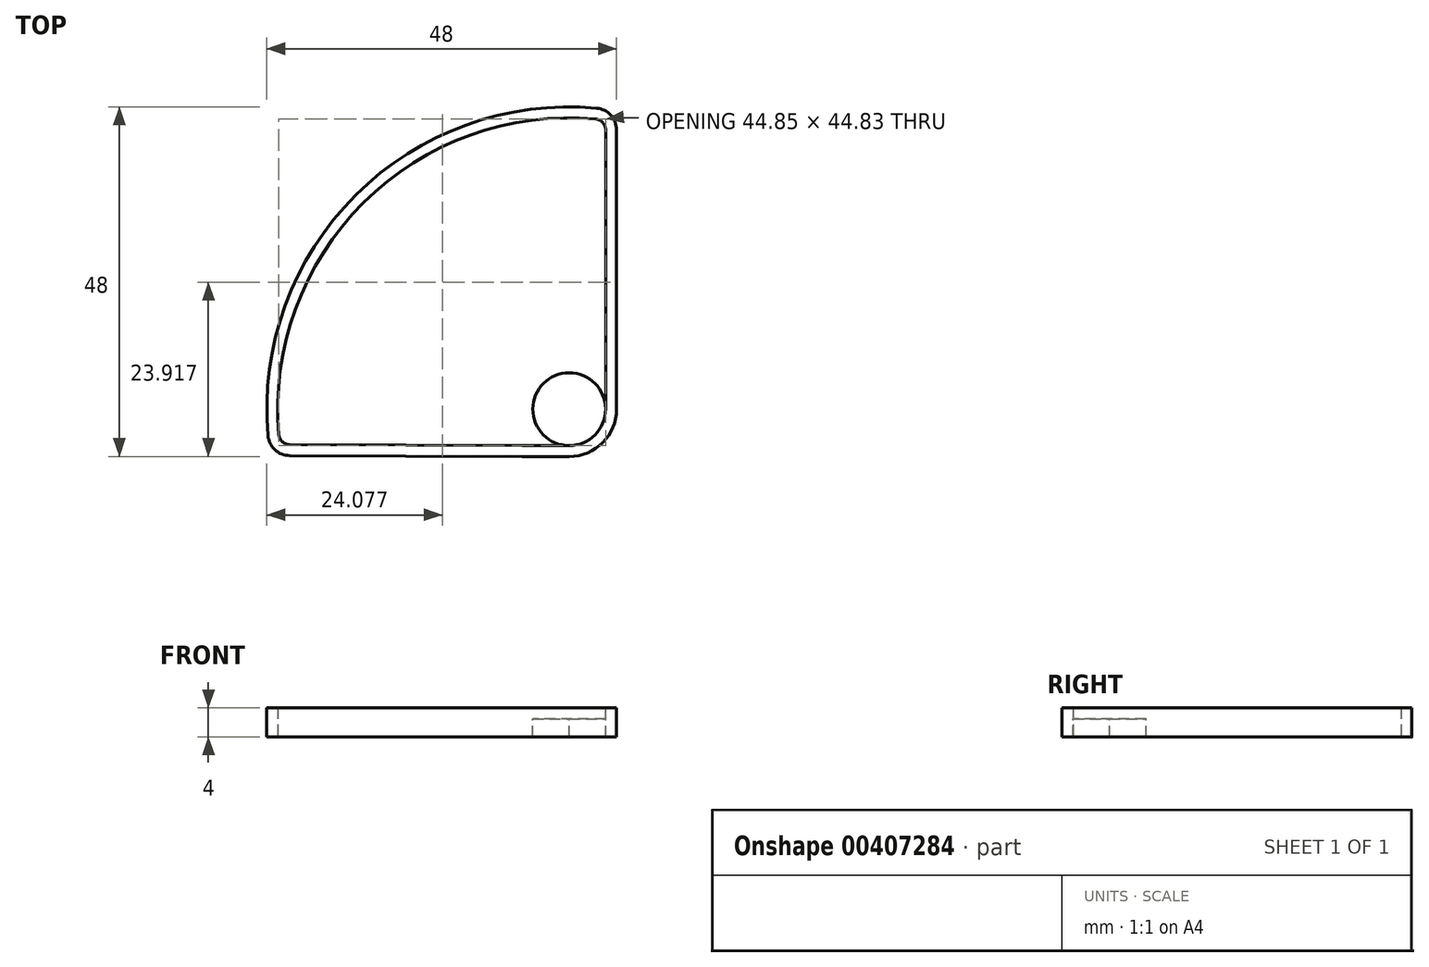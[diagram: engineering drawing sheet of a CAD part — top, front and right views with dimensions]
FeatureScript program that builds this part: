
annotation { "Feature Type Name" : "Feature", "Feature Type Description" : "" }
export const myFeature = defineFeature(function(context is Context, id is Id, definition is map)
    precondition{}
    {
        {
            var Q0;
            Q0=qCreatedBy(makeId("Top.planeOp"),FACE);
            var sketch = newSketch(context, id + "F0", { "sketchPlane" : qUnion([Q0])});
            skLineSegment(sketch, "E0", {"start": v(0, 6.5) * mm, "end": v(0, 47.49) * mm});
            skLineSegment(sketch, "E1.trimOffspring", {"start": v(-13, 0) * mm, "end": v(-47.5, 0.14) * mm});
            skLineSegment(sketch, "E2", {"start": v(-13, 0) * mm, "end": v(-6.5, 0) * mm});
            skPoint(sketch, "E3.visualSharp", {"position": v(0, 0) * mm});
            skArc(sketch, "E3.filletArc", {"start": v(-6.5, 0) * mm, "mid": v(-1.9, 1.9) * mm, "end": v(0, 6.5) * mm});
            skLineSegment(sketch, "E4", {"start": v(-6.5, 0) * mm, "end": v(-6.5, 12.92) * mm, "construction": true});
            skLineSegment(sketch, "E5", {"start": v(0, 6.5) * mm, "end": v(-6.5, 6.5) * mm, "construction": true});
            skArc(sketch, "E6", {"start": v(-47.5, 0.14) * mm, "mid": v(-35.8, 35.9) * mm, "end": v(0, 47.49) * mm});
            skSolve(sketch);
        }
        {
            var Q0;
            Q0=makeQuery(id+"F0.imprint","IMPRINT",FACE,{"disambiguationData":[TD([[makeQuery(id+"F0.imprint","IMPRINT",EDGE,{"derivedFrom":sQuery(id+"F0.wireOp",EDGE,"E0")}),1.0]])]});
            extrude(context, id + "F1", {"entities" : qUnion([Q0]), "depth" : 4 * mm});
        }
        {
            var Q0;
            Q0=makeQuery(id+"F1.opExtrude","CAP_FACE",FACE,{"disambiguationData":[OSD([sQuery(id+"F0.wireOp",EDGE,"NLBvzQAC-VEYf-z00a-SUDr-PS6Iiug7ZcWT"),sQuery(id+"F0.wireOp",EDGE,"vp4aBCBo-WHFW-VkR4-K5s5-xs8t65EtAtv6"),sQuery(id+"F0.wireOp",EDGE,"E0")])],"isStart":false});
            var Q1;
            Q1=makeQuery(id+"F1.opExtrude","CAP_FACE",FACE,{"disambiguationData":[OSD([sQuery(id+"F0.wireOp",EDGE,"NLBvzQAC-VEYf-z00a-SUDr-PS6Iiug7ZcWT"),sQuery(id+"F0.wireOp",EDGE,"E0"),sQuery(id+"F0.wireOp",EDGE,"sY9fAtrw-aqXI-RMX0-P5VE-8Oq5YwFjua6t"),sQuery(id+"F0.wireOp",EDGE,"E1.trimOffspring")])],"isStart":true});
            shell(context, id + "F2", {"entities" : qUnion([Q0, Q1]), "thickness" : 1.5 * mm});
        }
        {
            var Q0;
            Q0=qCreatedBy(makeId("Top.planeOp"),FACE);
            cPlane(context, id + "F3", {"entities" : qUnion([Q0]), "cplaneType" : CPlaneType.OFFSET, "offset" : 2.5 * mm, "width" : 150 * mm, "height" : 150 * mm});
        }
        {
            var Q0;
            Q0=qCreatedBy(id+"F3.planeOp",FACE);
            var sketch = newSketch(context, id + "F4", { "sketchPlane" : qUnion([Q0])});
            skLineSegment(sketch, "E7.0", {"start": v(-13, 1.5) * mm, "end": v(-46.2, 1.63) * mm});
            skLineSegment(sketch, "E8.0", {"start": v(-13, 1.5) * mm, "end": v(-6.5, 1.5) * mm});
            skArc(sketch, "E9.0", {"start": v(-6.5, 1.5) * mm, "mid": v(-2.96, 2.96) * mm, "end": v(-1.5, 6.5) * mm});
            skLineSegment(sketch, "E10.0", {"start": v(-1.5, 6.5) * mm, "end": v(-1.5, 46.19) * mm});
            skArc(sketch, "E11.0", {"start": v(-46.2, 1.63) * mm, "mid": v(-34.74, 34.83) * mm, "end": v(-1.5, 46.19) * mm});
            skSolve(sketch);
        }
        {
            var Q0;
            Q0=makeQuery(id+"F4.imprint","IMPRINT",FACE,{"disambiguationData":[TD([[makeQuery(id+"F4.imprint","IMPRINT",EDGE,{"derivedFrom":sQuery(id+"F4.wireOp",EDGE,"E7.0")}),-1.0]])]});
            extrude(context, id + "F5", {"entities" : qUnion([Q0]), "operationType" : NewBodyOperationType.ADD, "oppositeDirection" : true, "depth" : 2.5 * mm});
        }
        {
            var Q0;
            Q0=makeQuery(id+"F1.opExtrude","CAP_FACE",FACE,{"disambiguationData":[OSD([sQuery(id+"F0.wireOp",EDGE,"NLBvzQAC-VEYf-z00a-SUDr-PS6Iiug7ZcWT"),sQuery(id+"F0.wireOp",EDGE,"E0"),sQuery(id+"F0.wireOp",EDGE,"sY9fAtrw-aqXI-RMX0-P5VE-8Oq5YwFjua6t"),sQuery(id+"F0.wireOp",EDGE,"E1.trimOffspring")])],"isStart":false});
            var sketch = newSketch(context, id + "F6", { "sketchPlane" : qUnion([Q0])});
            skArc(sketch, "E12", {"start": v(-6.5, 1.5) * mm, "mid": v(-10.04, 10.04) * mm, "end": v(-1.5, 6.5) * mm});
            skArc(sketch, "E13", {"start": v(-6.5, 1.5) * mm, "mid": v(-2.96, 2.96) * mm, "end": v(-1.5, 6.5) * mm});
            skSolve(sketch);
        }
        {
            var Q0;
            Q0=makeQuery(id+"F6.imprint","IMPRINT",FACE,{"disambiguationData":[TD([[makeQuery(id+"F6.imprint","IMPRINT",EDGE,{"derivedFrom":sQuery(id+"F6.wireOp",EDGE,"2423aa4e-c1d6-4c93-982e-63635b142349.0.2")}),1.0]])]});
            var Q1;
            Q1=makeQuery(id+"F6.imprint","IMPRINT",FACE,{"disambiguationData":[TD([[makeQuery(id+"F6.imprint","IMPRINT",EDGE,{"derivedFrom":sQuery(id+"F6.wireOp",EDGE,"E12")}),-1.0]])]});
            extrude(context, id + "F7", {"entities" : qUnion([Q0, Q1]), "operationType" : NewBodyOperationType.REMOVE, "endBound" : BoundingType.THROUGH_ALL, "oppositeDirection" : true, "depth" : 25 * mm});
        }
        {
            var Q0;
            Q0=makeQuery(id+"F1.opExtrude","SWEPT_EDGE",EDGE,{"disambiguationData":[OSD([sQuery(id+"F0.wireOp",EDGE,"E1.trimOffspring"),sQuery(id+"F0.wireOp",EDGE,"E6")])]});
            var Q1;
            Q1=makeQuery(id+"F1.opExtrude","SWEPT_EDGE",EDGE,{"disambiguationData":[OSD([sQuery(id+"F0.wireOp",EDGE,"E0"),sQuery(id+"F0.wireOp",EDGE,"E6")])]});
            fillet(context, id + "F8", {"entities" : qUnion([Q0, Q1]), "radius" : 3 * mm, "tangentPropagation" : true, "allowEdgeOverflow" : false});
        }
        {
            var Q0;
            Q0=makeQuery(id+"F1.opExtrude","SWEPT_EDGE",EDGE,{"disambiguationData":[OSD([sQuery(id+"F0.wireOp",EDGE,"sY9fAtrw-aqXI-RMX0-P5VE-8Oq5YwFjua6t"),sQuery(id+"F0.wireOp",EDGE,"E1.trimOffspring")])]});
            var Q1;
            Q1=makeQuery(id+"F2.opShell","OFFSET_EDGE",EDGE,{"disambiguationData":[OSD([sQuery(id+"F0.wireOp",EDGE,"E1.trimOffspring"),sQuery(id+"F0.wireOp",EDGE,"E6")])]});
            var Q2;
            Q2=makeQuery(id+"F2.opShell","OFFSET_EDGE",EDGE,{"disambiguationData":[OSD([sQuery(id+"F0.wireOp",EDGE,"E0"),sQuery(id+"F0.wireOp",EDGE,"E6")])]});
            fillet(context, id + "F9", {"entities" : qUnion([Q0, Q1, Q2]), "radius" : 1.5 * mm, "tangentPropagation" : true, "allowEdgeOverflow" : false});
        }
    });
